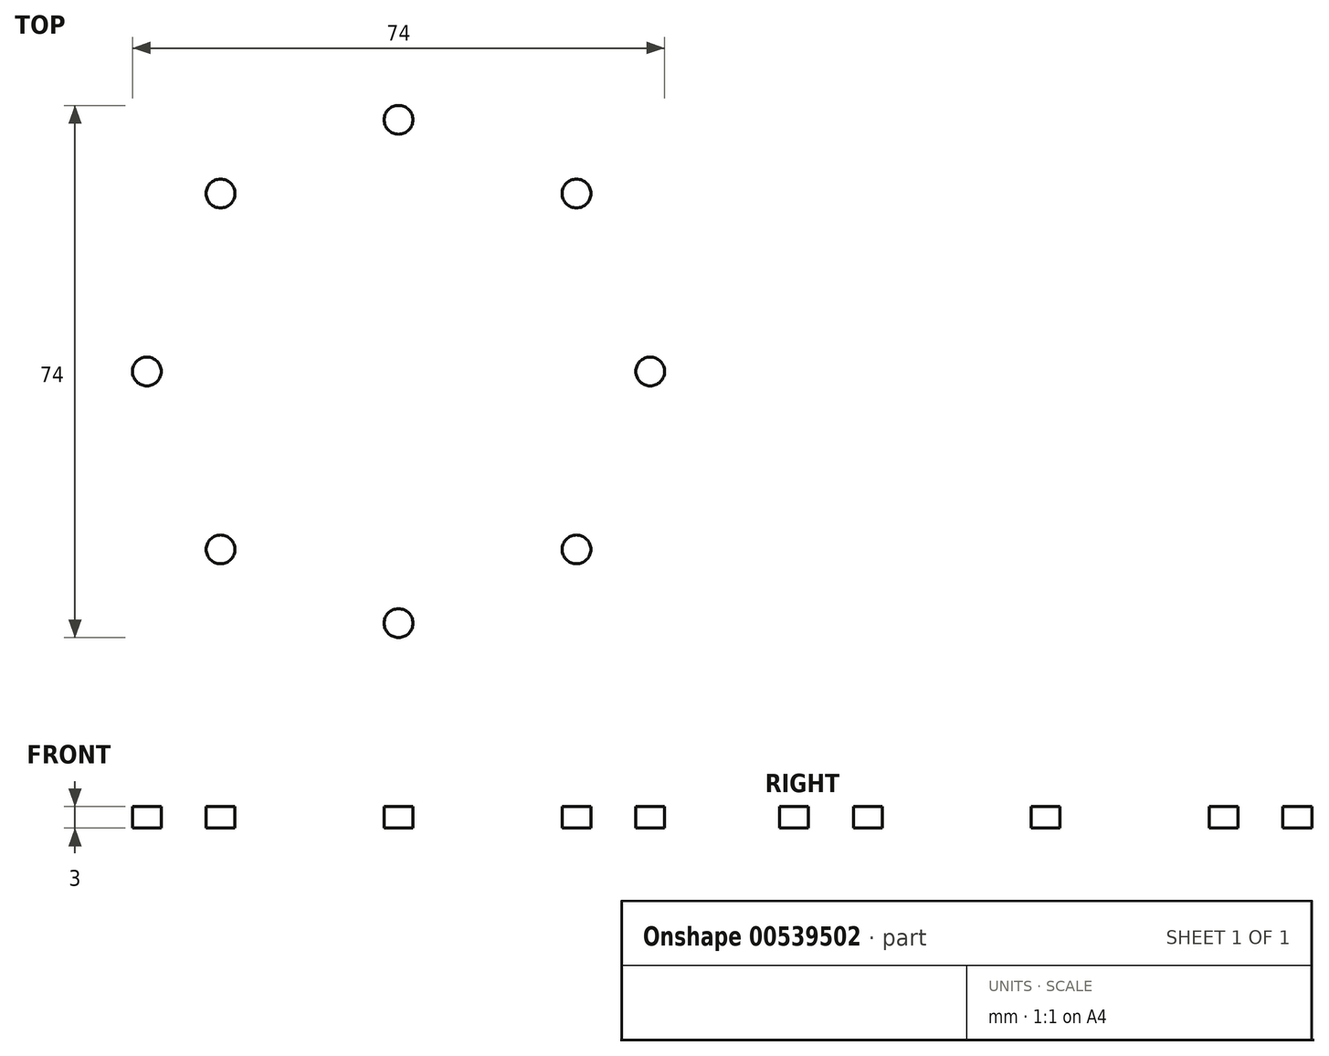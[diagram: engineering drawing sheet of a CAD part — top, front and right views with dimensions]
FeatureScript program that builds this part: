
annotation { "Feature Type Name" : "Feature", "Feature Type Description" : "" }
export const myFeature = defineFeature(function(context is Context, id is Id, definition is map)
    precondition{}
    {
        {
            var Q0;
            Q0=qCreatedBy(makeId("Front.planeOp"),FACE);
            var sketch = newSketch(context, id + "F0", { "sketchPlane" : qUnion([Q0])});
            skLineSegment(sketch, "E0", {"start": v(-44.5, 0) * mm, "end": v(-44.5, -8) * mm});
            skLineSegment(sketch, "E1", {"start": v(-44.5, -8) * mm, "end": v(-40.5, -8) * mm});
            skLineSegment(sketch, "E2", {"start": v(-40.5, -8) * mm, "end": v(-40.5, -16) * mm});
            skLineSegment(sketch, "E3", {"start": v(-40.5, -16) * mm, "end": v(-37.5, -16) * mm});
            skLineSegment(sketch, "E4", {"start": v(-37.5, -16) * mm, "end": v(-37.5, -8) * mm});
            skLineSegment(sketch, "E5", {"start": v(-37.5, -8) * mm, "end": v(-8, -8) * mm});
            skLineSegment(sketch, "E6", {"start": v(-8, -8) * mm, "end": v(-8, -5) * mm});
            skLineSegment(sketch, "E7", {"start": v(-8, -5) * mm, "end": v(-41.5, -5) * mm});
            skLineSegment(sketch, "E8", {"start": v(-41.5, -5) * mm, "end": v(-41.5, 0) * mm});
            skLineSegment(sketch, "E9", {"start": v(-41.5, 0) * mm, "end": v(-44.5, 0) * mm});
            skLineSegment(sketch, "E10", {"start": v(0, 8.2) * mm, "end": v(0, -19.52) * mm, "construction": true});
            skSolve(sketch);
        }
        {
            var Q0;
            Q0 = qConstructionFilter(qBodyType(qCreatedBy(id + "F0" ,EDGE), BodyType.WIRE), ConstructionObject.NO);
            var Q1;
            Q1=sQuery(id+"F0.wireOp",EDGE,"E10");
            revolve(context, id + "F1", {"bodyType" : ToolBodyType.SURFACE, "surfaceEntities" : qUnion([Q0]), "axis" : qUnion([Q1]), "revolveType" : RevolveType.FULL});
        }
        {
            var Q0;
            Q0=makeQuery(id+"F1.opRevolve","SWEPT_FACE",FACE,{"disambiguationData":[OSD([sQuery(id+"F0.wireOp",EDGE,"E7")])]});
            var sketch = newSketch(context, id + "F2", { "sketchPlane" : qUnion([Q0])});
            skCircle(sketch, "E11", {"center": v(0, -35) * mm, "radius": 2 * mm});
            skCircle(sketch, "E12.1.0", {"center": v(24.75, -24.75) * mm, "radius": 2 * mm});
            skCircle(sketch, "E12.2.0", {"center": v(35, 0) * mm, "radius": 2 * mm});
            skPoint(sketch, "E12.center", {"position": v(0, 0) * mm});
            skCircle(sketch, "E13.1.3.0", {"center": v(24.75, 24.75) * mm, "radius": 2 * mm});
            skCircle(sketch, "E14.1.4.0", {"center": v(0, 35) * mm, "radius": 2 * mm});
            skCircle(sketch, "E14.1.5.0", {"center": v(-24.75, 24.75) * mm, "radius": 2 * mm});
            skCircle(sketch, "E14.1.6.0", {"center": v(-35, 0) * mm, "radius": 2 * mm});
            skCircle(sketch, "E14.1.7.0", {"center": v(-24.75, -24.75) * mm, "radius": 2 * mm});
            skSolve(sketch);
        }
        {
            var Q0;
            Q0 = qSketchRegion(id + "F2", true);
            extrude(context, id + "F3", {"entities" : qUnion([Q0]), "oppositeDirection" : true, "depth" : 3 * mm, "offsetDistance" : 25 * mm});
        }
        {
            var Q0;
            Q0=makeQuery(id+"F1.opRevolve","SWEPT_FACE",FACE,{"disambiguationData":[OSD([sQuery(id+"F0.wireOp",EDGE,"E7")])]});
            fillet(context, id + "F4", {"entities" : qUnion([Q0]), "radius" : .5 * mm, "tangentPropagation" : true, "allowEdgeOverflow" : false});
        }
        {
            var Q0;
            Q0=makeQuery(id+"F1.opRevolve","SWEPT_FACE",FACE,{"disambiguationData":[OSD([sQuery(id+"F0.wireOp",EDGE,"E5")])]});
            var Q1;
            Q1=makeQuery(id+"F1.opRevolve","SWEPT_EDGE",EDGE,{"disambiguationData":[OSD([sQuery(id+"F0.wireOp",VERTEX,"E9.start")])]});
            fillet(context, id + "F5", {"entities" : qUnion([Q0, Q1]), "radius" : 2 * mm, "tangentPropagation" : true, "allowEdgeOverflow" : false});
        }
        {
            var Q0;
            Q0=makeQuery(id+"F1.opRevolve","SWEPT_EDGE",EDGE,{"disambiguationData":[OSD([sQuery(id+"F0.wireOp",VERTEX,"E2.start")])]});
            fillet(context, id + "F6", {"entities" : qUnion([Q0]), "radius" : .25 * mm, "tangentPropagation" : true, "allowEdgeOverflow" : false});
        }
    });
